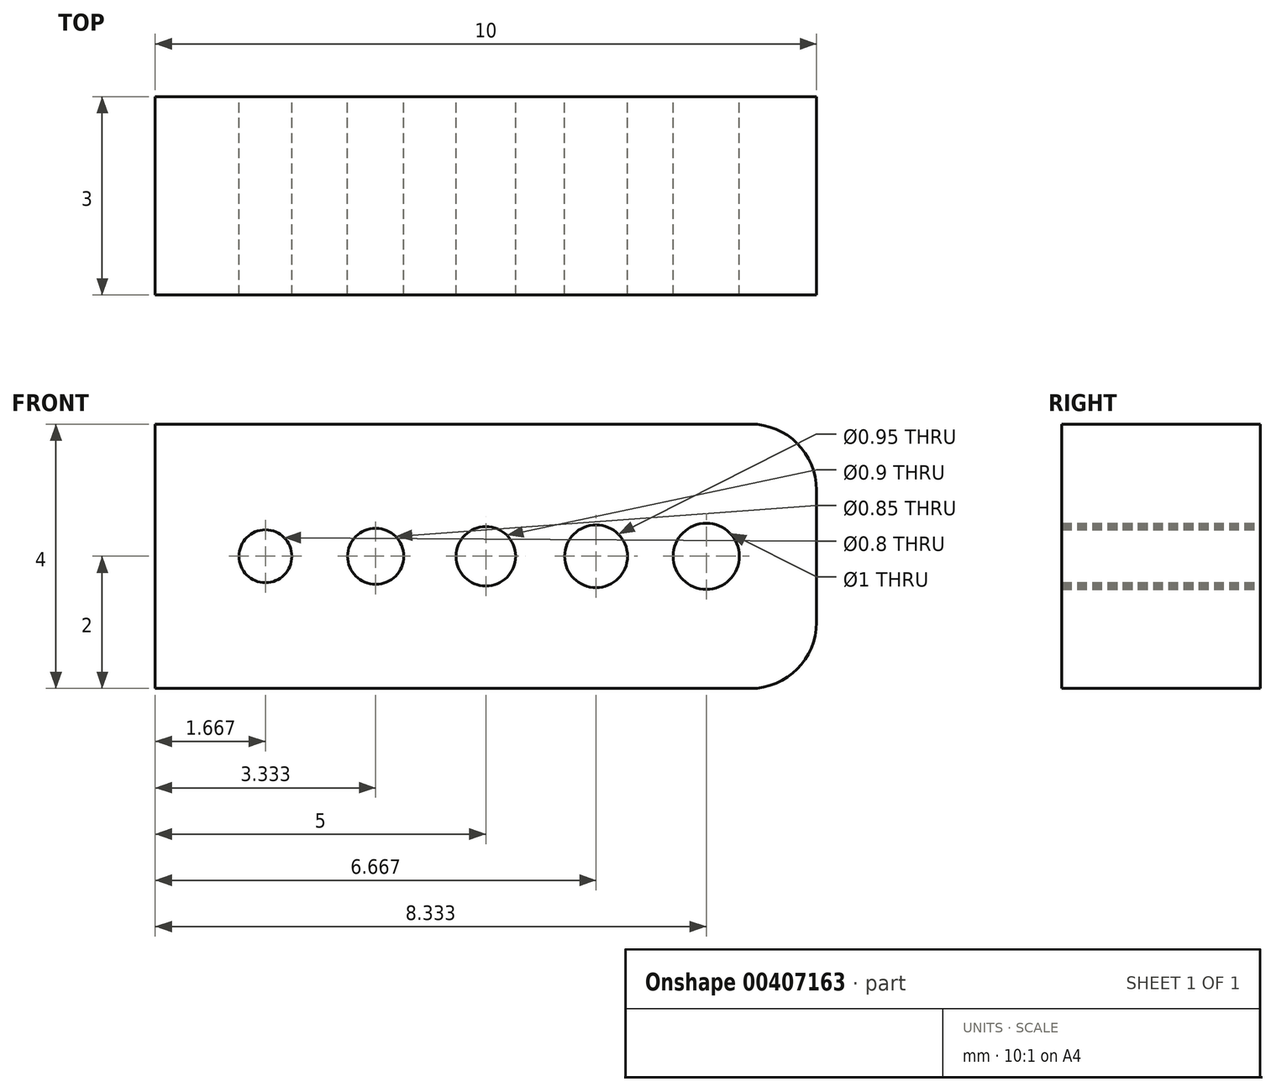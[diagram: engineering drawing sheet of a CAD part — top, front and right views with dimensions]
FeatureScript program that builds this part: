
annotation { "Feature Type Name" : "Feature", "Feature Type Description" : "" }
export const myFeature = defineFeature(function(context is Context, id is Id, definition is map)
    precondition{}
    {
        {
            var Q0;
            Q0=qCreatedBy(makeId("Front.planeOp"),FACE);
            var sketch = newSketch(context, id + "F0", { "sketchPlane" : qUnion([Q0])});
            skLineSegment(sketch, "E0.bottom", {"start": v(5, 2) * mm, "end": v(-5, 2) * mm});
            skLineSegment(sketch, "E0.top", {"start": v(5, -2) * mm, "end": v(-5, -2) * mm});
            skLineSegment(sketch, "E0.left", {"start": v(5, 2) * mm, "end": v(5, -2) * mm});
            skLineSegment(sketch, "E0.right", {"start": v(-5, 2) * mm, "end": v(-5, -2) * mm});
            skPoint(sketch, "E0.middle", {"position": v(0, 0) * mm});
            skLineSegment(sketch, "E1", {"start": v(-5, 0) * mm, "end": v(-3.33, 0) * mm, "construction": true});
            skLineSegment(sketch, "E2", {"start": v(-3.33, 0) * mm, "end": v(-1.67, 0) * mm, "construction": true});
            skLineSegment(sketch, "E3", {"start": v(-1.67, 0) * mm, "end": v(0, 0) * mm, "construction": true});
            skLineSegment(sketch, "E4", {"start": v(1.67, 0) * mm, "end": v(3.33, 0) * mm, "construction": true});
            skLineSegment(sketch, "E5", {"start": v(3.33, 0) * mm, "end": v(5, 0) * mm, "construction": true});
            skCircle(sketch, "E6", {"center": v(-3.33, 0) * mm, "radius": 0.4 * mm});
            skCircle(sketch, "E7", {"center": v(-1.67, 0) * mm, "radius": 0.42 * mm});
            skCircle(sketch, "E8", {"center": v(0, 0) * mm, "radius": 0.45 * mm});
            skCircle(sketch, "E9", {"center": v(1.67, 0) * mm, "radius": 0.47 * mm});
            skCircle(sketch, "E10", {"center": v(3.33, 0) * mm, "radius": 0.5 * mm});
            skSolve(sketch);
        }
        {
            var Q0;
            Q0 = qSketchRegion(id + "F0", true);
            extrude(context, id + "F1", {"entities" : qUnion([Q0]), "depth" : 3 * mm});
        }
        {
            var Q0;
            Q0=makeQuery(id+"F1.opExtrude","SWEPT_EDGE",EDGE,{"disambiguationData":[OSD([sQuery(id+"F0.wireOp",EDGE,"E0.bottom"),sQuery(id+"F0.wireOp",EDGE,"E0.left")])]});
            var Q1;
            Q1=makeQuery(id+"F1.opExtrude","SWEPT_EDGE",EDGE,{"disambiguationData":[OSD([sQuery(id+"F0.wireOp",EDGE,"E0.top"),sQuery(id+"F0.wireOp",EDGE,"E0.left")])]});
            fillet(context, id + "F2", {"entities" : qUnion([Q0, Q1]), "radius" : 1 * mm, "tangentPropagation" : true, "allowEdgeOverflow" : false});
        }
    });
